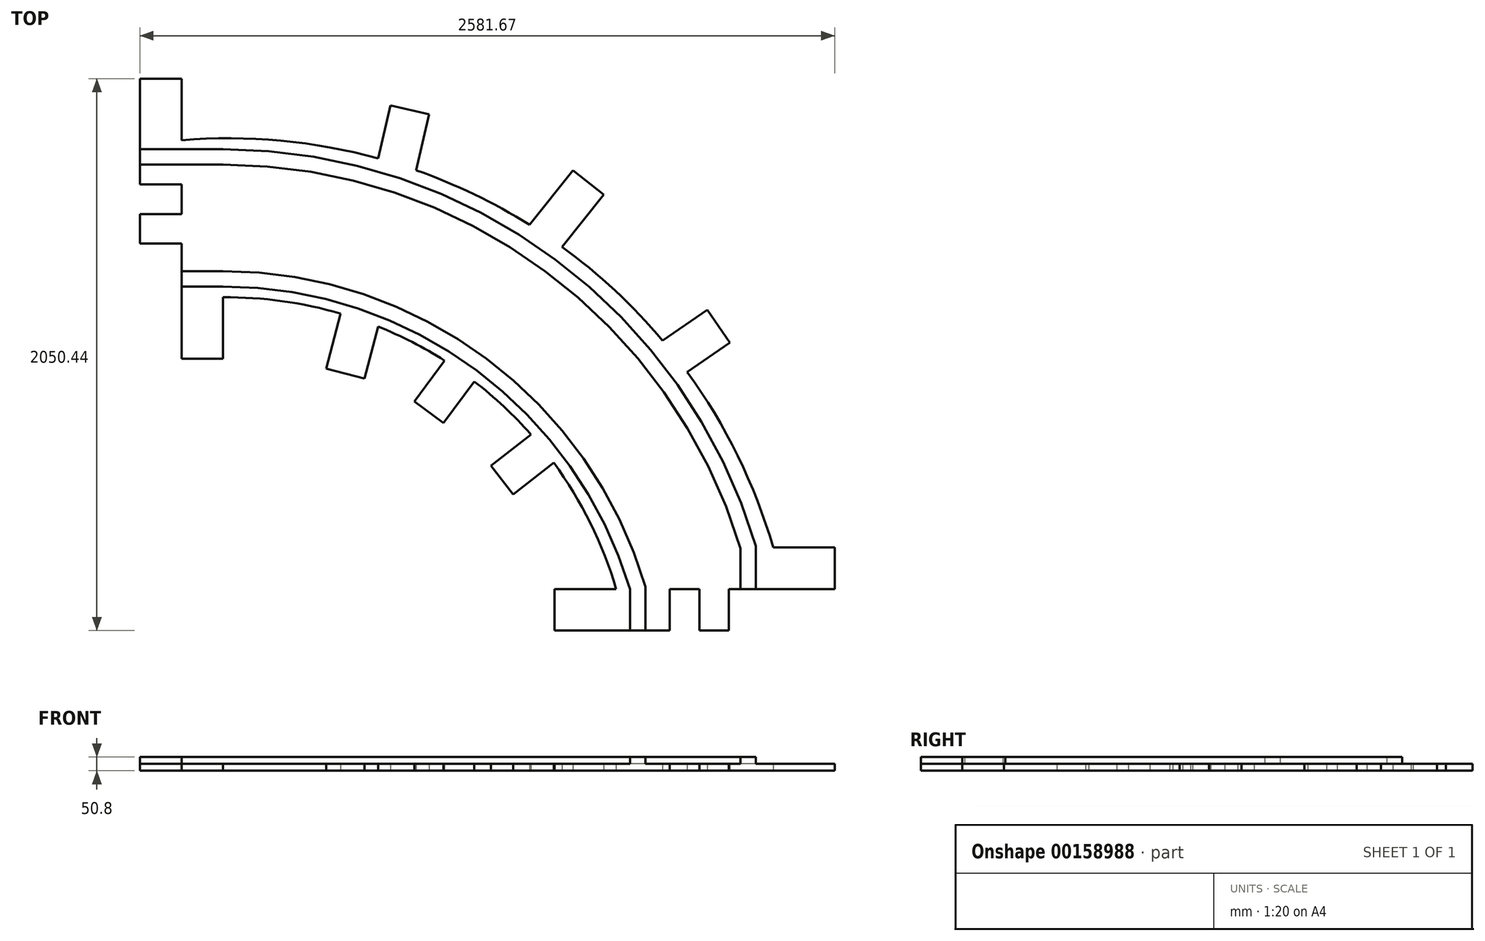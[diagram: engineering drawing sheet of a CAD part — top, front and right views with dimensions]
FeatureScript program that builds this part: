
annotation { "Feature Type Name" : "Feature", "Feature Type Description" : "" }
export const myFeature = defineFeature(function(context is Context, id is Id, definition is map)
    precondition{}
    {
        {
            var Q0;
            Q0=qCreatedBy(makeId("Top.planeOp"),FACE);
            var sketch = newSketch(context, id + "F0", { "sketchPlane" : qUnion([Q0])});
            skLineSegment(sketch, "E0", {"start": v(-123.12, 340.2) * mm, "end": v(-123.12, -52.81) * mm});
            skLineSegment(sketch, "E1", {"start": v(-123.12, -52.81) * mm, "end": v(31.19, -52.81) * mm});
            skLineSegment(sketch, "E2", {"start": v(31.19, -52.81) * mm, "end": v(31.19, -162.82) * mm});
            skLineSegment(sketch, "E3", {"start": v(31.19, -162.82) * mm, "end": v(-123.12, -162.82) * mm});
            skLineSegment(sketch, "E4", {"start": v(-123.12, -162.82) * mm, "end": v(-123.12, -272.82) * mm});
            skLineSegment(sketch, "E5", {"start": v(-123.12, -272.82) * mm, "end": v(31.19, -272.82) * mm});
            skLineSegment(sketch, "E6", {"start": v(31.19, -272.82) * mm, "end": v(31.19, -700.69) * mm});
            skLineSegment(sketch, "E7", {"start": v(2458.55, -1555.94) * mm, "end": v(2065.54, -1555.94) * mm});
            skLineSegment(sketch, "E8", {"start": v(2065.54, -1555.94) * mm, "end": v(2065.54, -1710.24) * mm});
            skLineSegment(sketch, "E9", {"start": v(2065.54, -1710.24) * mm, "end": v(1955.53, -1710.24) * mm});
            skLineSegment(sketch, "E10", {"start": v(1955.53, -1710.24) * mm, "end": v(1955.53, -1555.94) * mm});
            skLineSegment(sketch, "E11", {"start": v(1955.53, -1555.94) * mm, "end": v(1845.52, -1555.94) * mm});
            skLineSegment(sketch, "E12", {"start": v(1845.52, -1555.94) * mm, "end": v(1845.52, -1710.24) * mm});
            skLineSegment(sketch, "E13", {"start": v(1845.52, -1710.24) * mm, "end": v(1417.66, -1710.24) * mm});
            skLineSegment(sketch, "E14", {"start": v(-123.12, 340.2) * mm, "end": v(31.19, 340.2) * mm});
            skLineSegment(sketch, "E15", {"start": v(31.19, 340.2) * mm, "end": v(31.19, 111.7) * mm});
            skLineSegment(sketch, "E16", {"start": v(2458.55, -1555.94) * mm, "end": v(2458.55, -1401.63) * mm});
            skLineSegment(sketch, "E17", {"start": v(2458.55, -1401.63) * mm, "end": v(2230.06, -1401.63) * mm});
            skLineSegment(sketch, "E18", {"start": v(31.19, -700.69) * mm, "end": v(185.5, -700.69) * mm});
            skLineSegment(sketch, "E19", {"start": v(185.5, -700.69) * mm, "end": v(185.5, -472.19) * mm});
            skLineSegment(sketch, "E20", {"start": v(1417.66, -1710.24) * mm, "end": v(1417.66, -1555.94) * mm});
            skLineSegment(sketch, "E21", {"start": v(1417.66, -1555.94) * mm, "end": v(1646.16, -1555.94) * mm});
            skArc(sketch, "E22", {"start": v(2230.06, -1401.63) * mm, "mid": v(1400.55, -252.77) * mm, "end": v(31.19, 111.7) * mm});
            skArc(sketch, "E23", {"start": v(1646.16, -1555.94) * mm, "mid": v(1097.84, -768.75) * mm, "end": v(185.5, -472.19) * mm});
            skLineSegment(sketch, "E24", {"start": v(622.9, -532.64) * mm, "end": v(569.25, -736.82) * mm});
            skLineSegment(sketch, "E25", {"start": v(569.25, -736.82) * mm, "end": v(711.49, -774.2) * mm});
            skLineSegment(sketch, "E26", {"start": v(711.49, -774.2) * mm, "end": v(762.28, -580.9) * mm});
            skLineSegment(sketch, "E27", {"start": v(1008.82, -707.53) * mm, "end": v(896.3, -858.64) * mm});
            skLineSegment(sketch, "E28", {"start": v(896.3, -858.64) * mm, "end": v(1004.64, -939.3) * mm});
            skLineSegment(sketch, "E29", {"start": v(1004.64, -939.3) * mm, "end": v(1119.46, -785.1) * mm});
            skLineSegment(sketch, "E30", {"start": v(1329.87, -981.94) * mm, "end": v(1180.76, -1097.54) * mm});
            skLineSegment(sketch, "E31", {"start": v(1180.76, -1097.54) * mm, "end": v(1263.3, -1204) * mm});
            skLineSegment(sketch, "E32", {"start": v(1263.3, -1204) * mm, "end": v(1414.4, -1086.87) * mm});
            skLineSegment(sketch, "E33", {"start": v(762.28, 43.92) * mm, "end": v(807.94, 241.05) * mm});
            skLineSegment(sketch, "E34", {"start": v(807.94, 241.05) * mm, "end": v(951.13, 207.94) * mm});
            skLineSegment(sketch, "E35", {"start": v(951.13, 207.94) * mm, "end": v(903.05, 0) * mm});
            skLineSegment(sketch, "E36", {"start": v(1324.29, -202.68) * mm, "end": v(1485.87, 0) * mm});
            skLineSegment(sketch, "E37", {"start": v(1485.87, 0) * mm, "end": v(1599.81, -90.84) * mm});
            skLineSegment(sketch, "E38", {"start": v(1599.81, -90.84) * mm, "end": v(1445.4, -284.5) * mm});
            skLineSegment(sketch, "E39", {"start": v(1819.14, -632.88) * mm, "end": v(1985.43, -518.5) * mm});
            skLineSegment(sketch, "E40", {"start": v(1985.43, -518.5) * mm, "end": v(2068.94, -639.9) * mm});
            skLineSegment(sketch, "E41", {"start": v(2068.94, -639.9) * mm, "end": v(1910.13, -749.14) * mm});
            skSolve(sketch);
        }
        {
            var Q0;
            Q0=qSketchRegion(id+"F0",true);
            extrude(context, id + "F1", {"entities" : qUnion([Q0]), "depth" : 25.4 * mm});
        }
        {
            var Q0;
            Q0=makeQuery(id+"F1.opExtrude","CAP_FACE",FACE,{"disambiguationData":[OSD([sQuery(id+"F0.wireOp",EDGE,"E0"),sQuery(id+"F0.wireOp",EDGE,"E1"),sQuery(id+"F0.wireOp",EDGE,"E2"),sQuery(id+"F0.wireOp",EDGE,"E3"),sQuery(id+"F0.wireOp",EDGE,"E4"),sQuery(id+"F0.wireOp",EDGE,"E5"),sQuery(id+"F0.wireOp",EDGE,"E6"),sQuery(id+"F0.wireOp",EDGE,"E7"),sQuery(id+"F0.wireOp",EDGE,"E8"),sQuery(id+"F0.wireOp",EDGE,"E9"),sQuery(id+"F0.wireOp",EDGE,"E10"),sQuery(id+"F0.wireOp",EDGE,"E11"),sQuery(id+"F0.wireOp",EDGE,"E12"),sQuery(id+"F0.wireOp",EDGE,"E13"),sQuery(id+"F0.wireOp",EDGE,"E14"),sQuery(id+"F0.wireOp",EDGE,"E15"),sQuery(id+"F0.wireOp",EDGE,"E16"),sQuery(id+"F0.wireOp",EDGE,"E17"),sQuery(id+"F0.wireOp",EDGE,"E18"),sQuery(id+"F0.wireOp",EDGE,"E19"),sQuery(id+"F0.wireOp",EDGE,"E20"),sQuery(id+"F0.wireOp",EDGE,"E21"),sQuery(id+"F0.wireOp",EDGE,"E22"),sQuery(id+"F0.wireOp",EDGE,"E23"),sQuery(id+"F0.wireOp",EDGE,"E24"),sQuery(id+"F0.wireOp",EDGE,"E25"),sQuery(id+"F0.wireOp",EDGE,"E26"),sQuery(id+"F0.wireOp",EDGE,"E27"),sQuery(id+"F0.wireOp",EDGE,"E28"),sQuery(id+"F0.wireOp",EDGE,"E29"),sQuery(id+"F0.wireOp",EDGE,"E30"),sQuery(id+"F0.wireOp",EDGE,"E31"),sQuery(id+"F0.wireOp",EDGE,"E32"),sQuery(id+"F0.wireOp",EDGE,"E33"),sQuery(id+"F0.wireOp",EDGE,"E34"),sQuery(id+"F0.wireOp",EDGE,"E35"),sQuery(id+"F0.wireOp",EDGE,"E36"),sQuery(id+"F0.wireOp",EDGE,"E37"),sQuery(id+"F0.wireOp",EDGE,"E38"),sQuery(id+"F0.wireOp",EDGE,"E39"),sQuery(id+"F0.wireOp",EDGE,"E40"),sQuery(id+"F0.wireOp",EDGE,"E41")])],"isStart":false});
            var sketch = newSketch(context, id + "F2", { "sketchPlane" : qUnion([Q0])});
            skLineSegment(sketch, "E42", {"start": v(31.19, -432.08) * mm, "end": v(185.43, -432.08) * mm});
            skLineSegment(sketch, "E43", {"start": v(-123.12, 77.71) * mm, "end": v(185.43, 77.71) * mm});
            skLineSegment(sketch, "E44", {"start": v(2165.73, -1555.94) * mm, "end": v(2165.73, -1396.56) * mm});
            skLineSegment(sketch, "E45", {"start": v(1697.89, -1710.24) * mm, "end": v(1697.89, -1555.94) * mm});
            skArc(sketch, "E46", {"start": v(1697.89, -1555.94) * mm, "mid": v(1127.58, -743.8) * mm, "end": v(185.43, -432.08) * mm});
            skArc(sketch, "E47", {"start": v(2165.73, -1396.56) * mm, "mid": v(1419.83, -331.32) * mm, "end": v(185.43, 77.71) * mm});
            skLineSegment(sketch, "E48.0", {"start": v(-123.12, 20.56) * mm, "end": v(185.43, 20.56) * mm});
            skArc(sketch, "E48.1", {"start": v(2108.58, -1404.99) * mm, "mid": v(1382.37, -374.69) * mm, "end": v(185.43, 20.56) * mm});
            skLineSegment(sketch, "E48.2", {"start": v(2108.58, -1555.94) * mm, "end": v(2108.58, -1404.99) * mm});
            skLineSegment(sketch, "E49.0", {"start": v(31.19, -374.93) * mm, "end": v(185.43, -374.93) * mm});
            skArc(sketch, "E49.1", {"start": v(1755.04, -1547.6) * mm, "mid": v(1165.07, -700.47) * mm, "end": v(185.43, -374.93) * mm});
            skLineSegment(sketch, "E49.2", {"start": v(1755.04, -1710.24) * mm, "end": v(1755.04, -1547.6) * mm});
            skLineSegment(sketch, "E50", {"start": v(31.19, -374.93) * mm, "end": v(31.19, -432.08) * mm});
            skLineSegment(sketch, "E51", {"start": v(-123.12, 77.71) * mm, "end": v(-123.12, 20.56) * mm});
            skLineSegment(sketch, "E52", {"start": v(1697.89, -1710.24) * mm, "end": v(1755.04, -1710.24) * mm});
            skLineSegment(sketch, "E53", {"start": v(2108.58, -1555.94) * mm, "end": v(2165.73, -1555.94) * mm});
            skLineSegment(sketch, "E54", {"start": v(31.19, -700.69) * mm, "end": v(31.19, -1710.24) * mm, "construction": true});
            skLineSegment(sketch, "E55", {"start": v(31.19, -1710.24) * mm, "end": v(1417.66, -1710.24) * mm, "construction": true});
            skSolve(sketch);
        }
        {
            var Q0;
            Q0=qSketchRegion(id+"F2",true);
            extrude(context, id + "F3", {"entities" : qUnion([Q0]), "operationType" : NewBodyOperationType.ADD, "depth" : 25.4 * mm});
        }
    });
